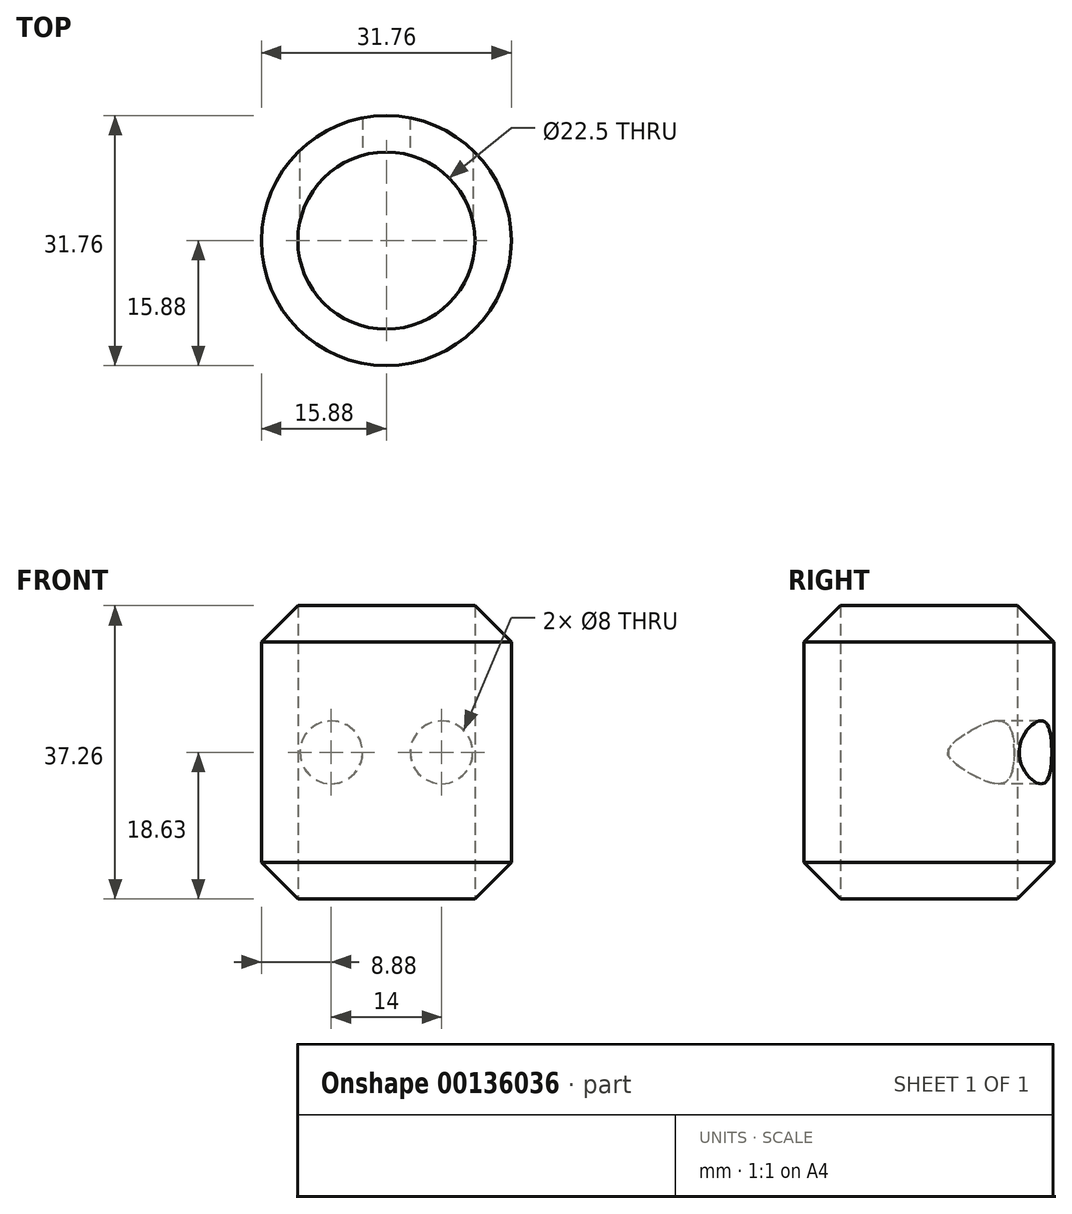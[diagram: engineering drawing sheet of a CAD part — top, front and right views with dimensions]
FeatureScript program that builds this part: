
annotation { "Feature Type Name" : "Feature", "Feature Type Description" : "" }
export const myFeature = defineFeature(function(context is Context, id is Id, definition is map)
    precondition{}
    {
        {
            var Q0;
            Q0=qCreatedBy(makeId("Top.planeOp"),FACE);
            var sketch = newSketch(context, id + "F0", { "sketchPlane" : qUnion([Q0])});
            skCircle(sketch, "E0", {"center": v(0, 0) * mm, "radius": 11.25 * mm});
            skCircle(sketch, "E1", {"center": v(0, 0) * mm, "radius": 15.88 * mm});
            skSolve(sketch);
        }
        {
            var Q0;
            Q0=qSketchRegion(id+"F0",true);
            extrude(context, id + "F1", {"entities" : qUnion([Q0]), "depth" : 38 * mm});
        }
        {
            var Q0;
            Q0=qCreatedBy(makeId("Front.planeOp"),FACE);
            var sketch = newSketch(context, id + "F2", { "sketchPlane" : qUnion([Q0])});
            skLineSegment(sketch, "E2", {"start": v(0, 0) * mm, "end": v(0, 38) * mm, "construction": true});
            skLineSegment(sketch, "E3", {"start": v(0, 38) * mm, "end": v(10, 38) * mm, "construction": true});
            skLineSegment(sketch, "E4", {"start": v(0, 0) * mm, "end": v(7, 0) * mm});
            skLineSegment(sketch, "E5.0", {"start": v(0, 19) * mm, "end": v(7, 19) * mm, "construction": true});
            skLineSegment(sketch, "E6.0", {"start": v(0, 12) * mm, "end": v(7, 12) * mm});
            skLineSegment(sketch, "E7.0", {"start": v(0, 26) * mm, "end": v(10, 26) * mm});
            skCircle(sketch, "E8", {"center": v(7, 19) * mm, "radius": 4 * mm});
            skCircle(sketch, "E9.MirrorC", {"center": v(-7, 19) * mm, "radius": 4 * mm});
            skSolve(sketch);
        }
        {
            var Q0;
            Q0=makeQuery(id+"F1.opExtrude","CAP_EDGE",EDGE,{"disambiguationData":[OSD([sQuery(id+"F0.wireOp",EDGE,"E1")])],"isStart":false});
            var Q1;
            Q1=makeQuery(id+"F1.opExtrude","CAP_EDGE",EDGE,{"disambiguationData":[OSD([sQuery(id+"F0.wireOp",EDGE,"E1")])],"isStart":true});
            chamfer(context, id + "F3", {"entities" : qUnion([Q0, Q1]), "width" : 5 * mm, "tangentPropagation" : true});
        }
        {
            var Q0;
            Q0 = qSketchRegion(id + "F2", true);
            extrude(context, id + "F4", {"entities" : qUnion([Q0]), "operationType" : NewBodyOperationType.REMOVE, "endBound" : BoundingType.THROUGH_ALL, "oppositeDirection" : true, "depth" : 25 * mm});
        }
    });
